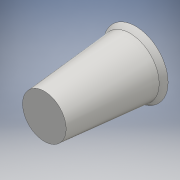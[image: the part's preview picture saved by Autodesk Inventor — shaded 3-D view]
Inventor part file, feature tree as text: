
AUTODESK INVENTOR PART (.ipt)
format: ipt  version: 2016 (Build 200138000, 138)  size: 122,880 bytes
history: native  units: mm
features: sketch x3, plane x2, loft x2, shell x1, other x1
ambient origin geometry x8: Origin, YZ Plane, XZ Plane, XY Plane, X Axis, Y Axis, Z Axis, Center Point
bodies: Solid1 (feature_tree)
feature tree (9):
  sketch  "Sketch1"  dims[d0=47.0mm d1=92.5mm]
  plane  "Work Plane1"
  sketch  "Sketch2"  dims[d2=62.75mm d3=98.5mm d4=70.0mm]
  plane  "Work Plane2"
  sketch  "Sketch3"  dims[d5=0.0mm d6=90.0deg d7=0.0mm d8=90.0deg d9=0.0mm d10=90.0deg d11=0.0mm d12=90.0deg d13=2.0mm]
  loft  "Loft1"
  loft  "Loft2"
  shell  "Shell1"  Thickness=70.0mm
  other  "Edges1"
